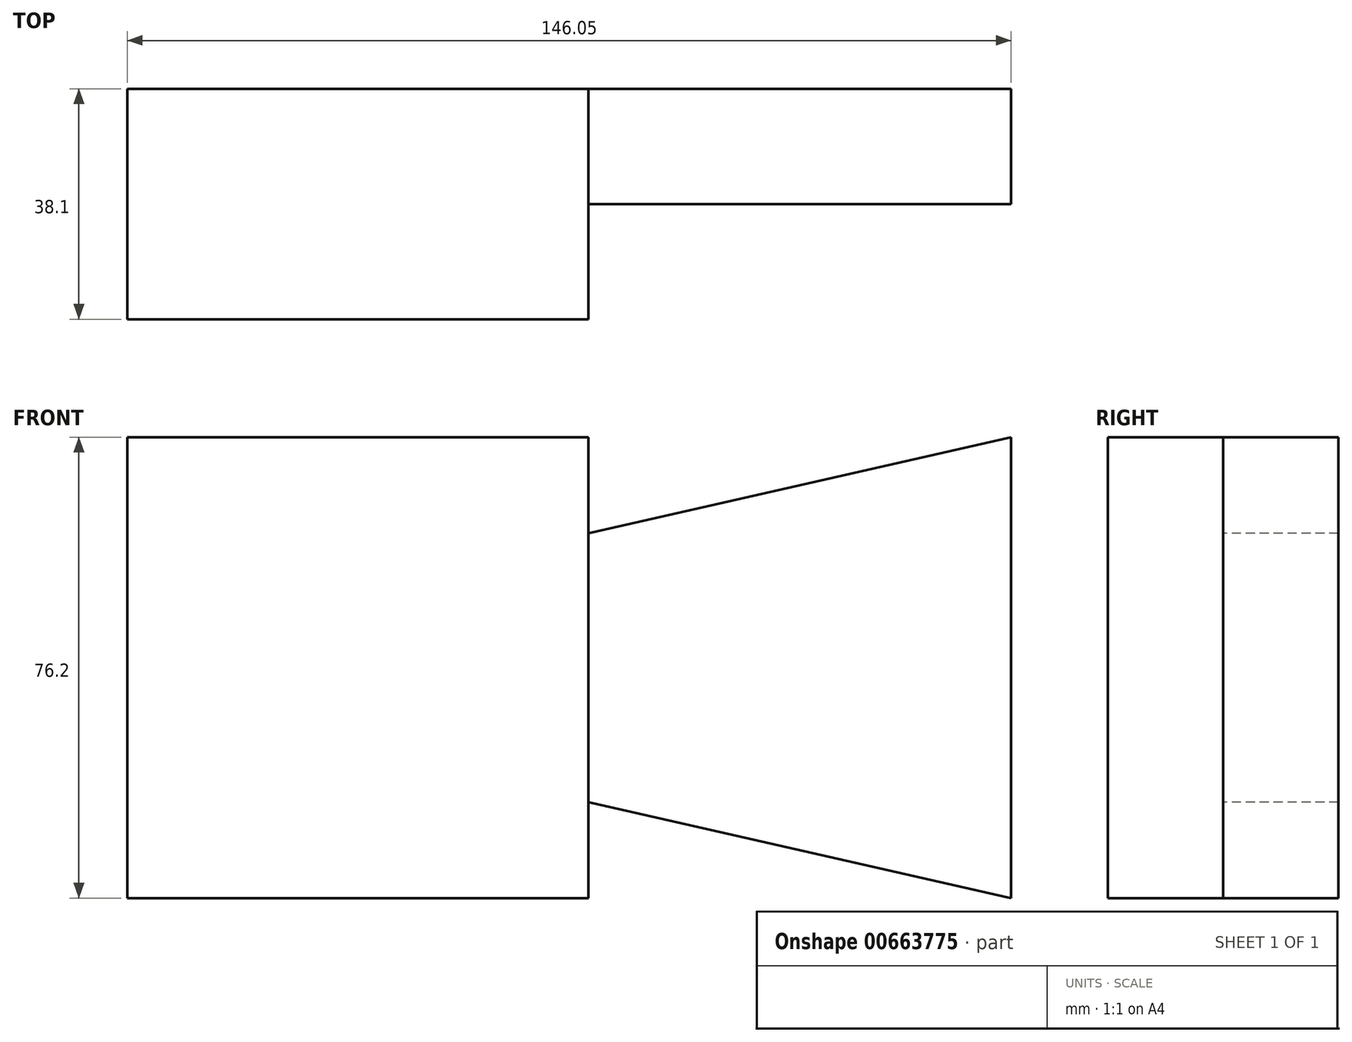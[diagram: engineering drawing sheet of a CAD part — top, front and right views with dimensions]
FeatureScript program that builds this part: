
annotation { "Feature Type Name" : "Feature", "Feature Type Description" : "" }
export const myFeature = defineFeature(function(context is Context, id is Id, definition is map)
    precondition{}
    {
        {
            var Q0;
            Q0=qCreatedBy(makeId("Front.planeOp"),FACE);
            var sketch = newSketch(context, id + "F0", { "sketchPlane" : qUnion([Q0])});
            skLineSegment(sketch, "E0.bottom", {"start": v(-64.53, 41.93) * mm, "end": v(11.67, 41.93) * mm});
            skLineSegment(sketch, "E0.top", {"start": v(-64.53, -34.27) * mm, "end": v(11.67, -34.27) * mm});
            skLineSegment(sketch, "E0.left", {"start": v(-64.53, 41.93) * mm, "end": v(-64.53, -34.27) * mm});
            skLineSegment(sketch, "E0.right", {"start": v(11.67, 41.93) * mm, "end": v(11.67, -34.27) * mm});
            skSolve(sketch);
        }
        {
            var Q0;
            Q0 = qSketchRegion(id + "F0", true);
            extrude(context, id + "F1", {"entities" : qUnion([Q0]), "depth" : 38.1 * mm, "offsetDistance" : 25.4 * mm});
        }
        {
            var Q0;
            Q0=makeQuery(id+"F1.opExtrude","SWEPT_FACE",FACE,{"disambiguationData":[OSD([sQuery(id+"F0.wireOp",EDGE,"E0.right")])]});
            var sketch = newSketch(context, id + "F2", { "sketchPlane" : qUnion([Q0])});
            skLineSegment(sketch, "E1.bottom", {"start": v(0, 26.06) * mm, "end": v(-19.05, 26.06) * mm});
            skLineSegment(sketch, "E1.top", {"start": v(0, -18.4) * mm, "end": v(-19.05, -18.4) * mm});
            skLineSegment(sketch, "E1.left", {"start": v(0, 26.06) * mm, "end": v(0, -18.4) * mm});
            skLineSegment(sketch, "E1.right", {"start": v(-19.05, 26.06) * mm, "end": v(-19.05, -18.4) * mm});
            skSolve(sketch);
        }
        {
            var Q0;
            Q0=makeQuery(id+"F2.imprint","IMPRINT",FACE,{"disambiguationData":[TD([[makeQuery(id+"F2.imprint","IMPRINT",EDGE,{"derivedFrom":sQuery(id+"F2.wireOp",EDGE,"E1.bottom")}),1.0]])]});
            extrude(context, id + "F3", {"entities" : qUnion([Q0]), "operationType" : NewBodyOperationType.ADD, "depth" : 69.85 * mm, "offsetDistance" : 25.4 * mm});
        }
        {
            var Q0;
            Q0=makeQuery(id+"F3.opExtrude","SWEPT_FACE",FACE,{"disambiguationData":[OSD([sQuery(id+"F2.wireOp",EDGE,"E1.right")])]});
            var sketch = newSketch(context, id + "F4", { "sketchPlane" : qUnion([Q0])});
            skLineSegment(sketch, "E2", {"start": v(11.67, 26.06) * mm, "end": v(81.52, 41.93) * mm});
            skLineSegment(sketch, "E3", {"start": v(81.52, 41.93) * mm, "end": v(81.52, 26.06) * mm});
            skLineSegment(sketch, "E4", {"start": v(81.52, 26.06) * mm, "end": v(81.52, -18.4) * mm});
            skLineSegment(sketch, "E5", {"start": v(81.52, -18.4) * mm, "end": v(81.52, -34.27) * mm});
            skLineSegment(sketch, "E6", {"start": v(81.52, -34.27) * mm, "end": v(11.67, -18.4) * mm});
            skSolve(sketch);
        }
        {
            var Q0;
            Q0=makeQuery(id+"F4.imprint","IMPRINT",FACE,{"disambiguationData":[TD([[makeQuery(id+"F4.imprint","IMPRINT",EDGE,{"derivedFrom":sQuery(id+"F4.wireOp",EDGE,"E2")}),-1.0]])]});
            var Q1;
            Q1=makeQuery(id+"F4.imprint","IMPRINT",FACE,{"disambiguationData":[TD([[makeQuery(id+"F4.imprint","IMPRINT",EDGE,{"derivedFrom":sQuery(id+"F4.wireOp",EDGE,"E5")}),-1.0]])]});
            extrude(context, id + "F5", {"entities" : qUnion([Q0, Q1]), "operationType" : NewBodyOperationType.ADD, "oppositeDirection" : true, "depth" : 19.05 * mm, "offsetDistance" : 25.4 * mm});
        }
    });
